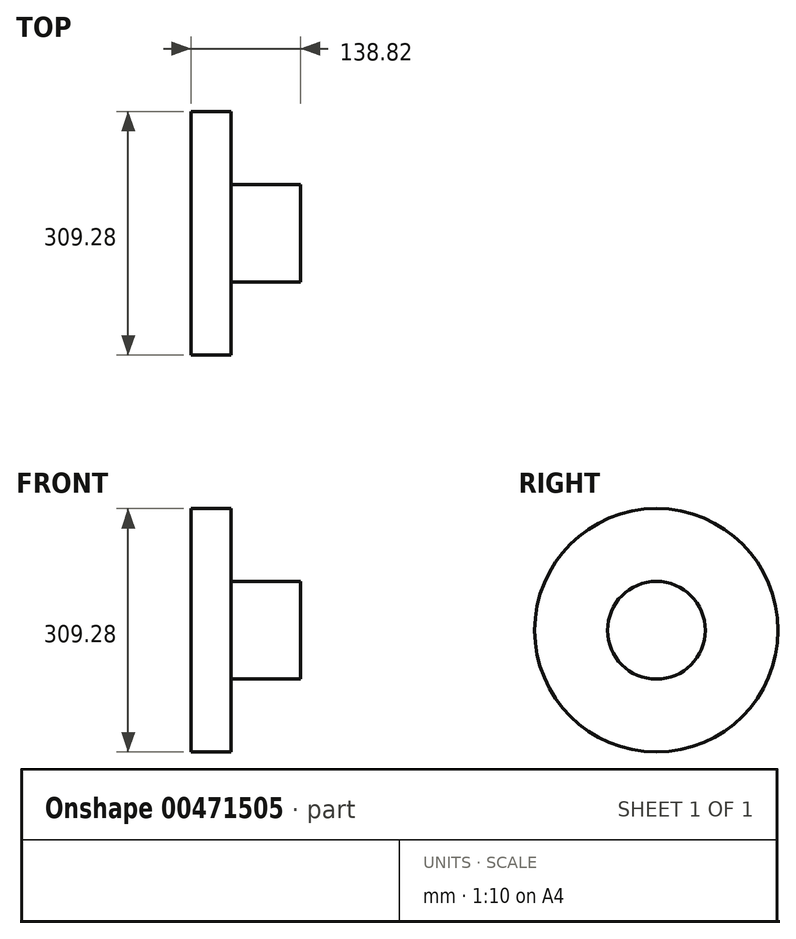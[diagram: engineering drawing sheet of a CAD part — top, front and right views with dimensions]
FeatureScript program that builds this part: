
annotation { "Feature Type Name" : "Feature", "Feature Type Description" : "" }
export const myFeature = defineFeature(function(context is Context, id is Id, definition is map)
    precondition{}
    {
        {
            var Q0;
            Q0=qCreatedBy(makeId("Right.planeOp"),FACE);
            var sketch = newSketch(context, id + "F0", { "sketchPlane" : qUnion([Q0])});
            skCircle(sketch, "E0", {"center": v(0, 0) * mm, "radius": 154.64 * mm});
            skSolve(sketch);
        }
        {
            var Q0;
            Q0 = qSketchRegion(id + "F0", true);
            extrude(context, id + "F1", {"entities" : qUnion([Q0]), "depth" : 50.8 * mm});
        }
        {
            var Q0;
            Q0=makeQuery(id+"F1.opExtrude","CAP_FACE",FACE,{"disambiguationData":[OSD([sQuery(id+"F0.wireOp",EDGE,"E0")])],"isStart":true});
            var sketch = newSketch(context, id + "F2", { "sketchPlane" : qUnion([Q0])});
            skCircle(sketch, "E1", {"center": v(0, 0) * mm, "radius": 62.08 * mm});
            skSolve(sketch);
        }
        {
            var Q0;
            Q0 = qSketchRegion(id + "F2", true);
            extrude(context, id + "F3", {"entities" : qUnion([Q0]), "operationType" : NewBodyOperationType.ADD, "oppositeDirection" : true, "depth" : 138.82 * mm});
        }
    });
